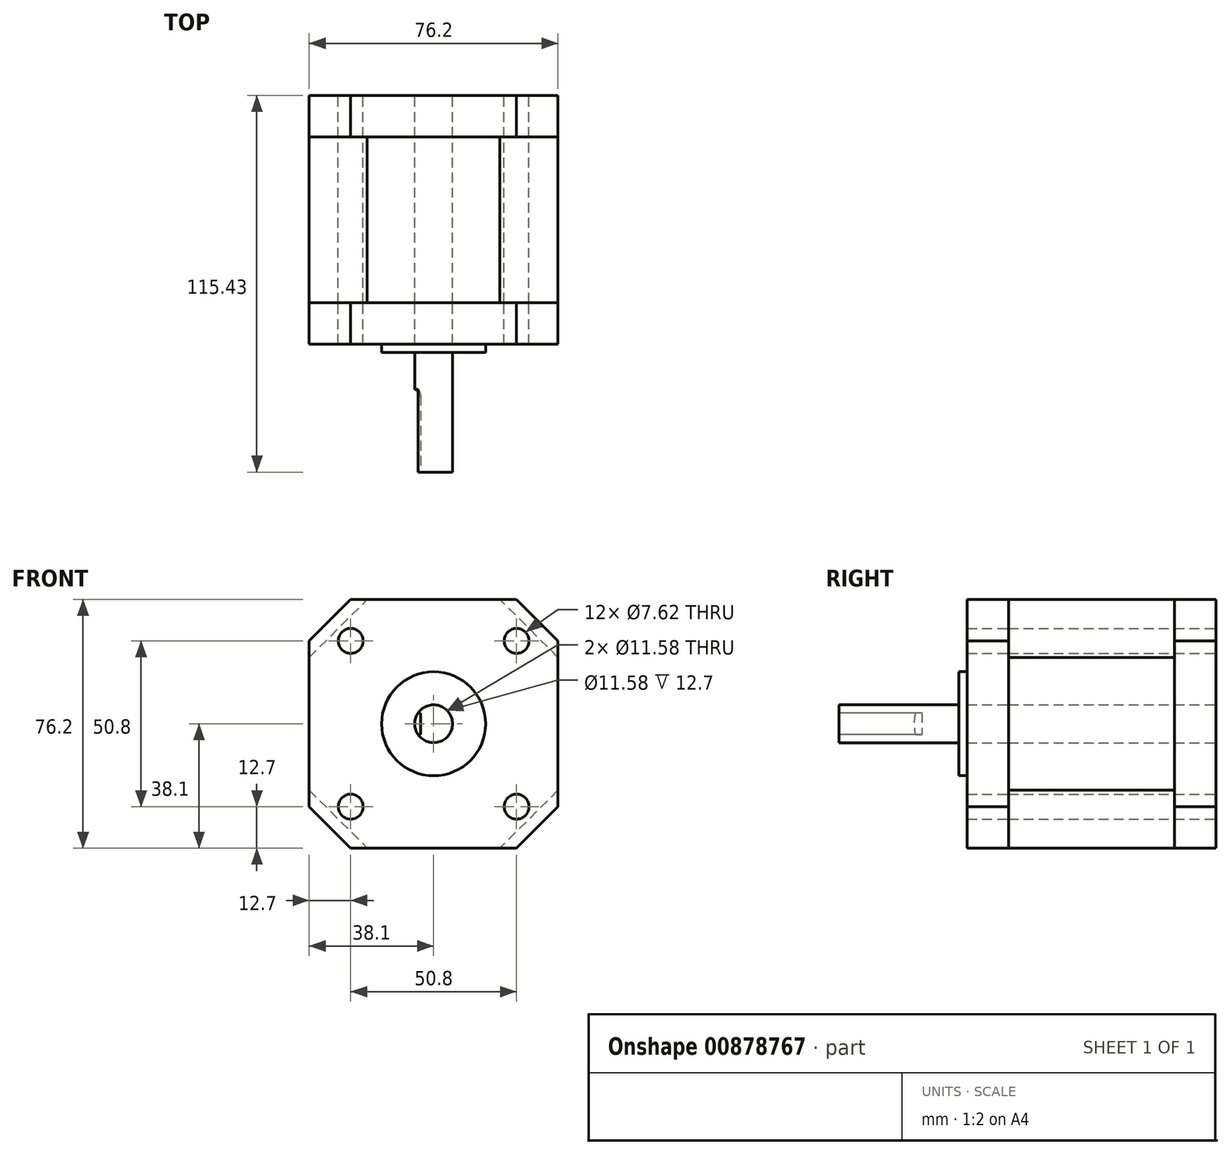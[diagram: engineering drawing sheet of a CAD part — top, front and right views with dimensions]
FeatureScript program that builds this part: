
annotation { "Feature Type Name" : "Feature", "Feature Type Description" : "" }
export const myFeature = defineFeature(function(context is Context, id is Id, definition is map)
    precondition{}
    {
        {
            var Q0;
            Q0=qCreatedBy(makeId("Front.planeOp"),FACE);
            var sketch = newSketch(context, id + "F0", { "sketchPlane" : qUnion([Q0])});
            skLineSegment(sketch, "E0.bottom", {"start": v(38.1, 38.1) * mm, "end": v(-38.1, 38.1) * mm});
            skLineSegment(sketch, "E0.top", {"start": v(38.1, -38.1) * mm, "end": v(-38.1, -38.1) * mm});
            skLineSegment(sketch, "E0.left", {"start": v(38.1, 38.1) * mm, "end": v(38.1, -38.1) * mm});
            skLineSegment(sketch, "E0.right", {"start": v(-38.1, 38.1) * mm, "end": v(-38.1, -38.1) * mm});
            skPoint(sketch, "E0.middle", {"position": v(0, 0) * mm});
            skLineSegment(sketch, "E1.bottom", {"start": v(25.4, -25.4) * mm, "end": v(-25.4, -25.4) * mm, "construction": true});
            skLineSegment(sketch, "E1.top", {"start": v(25.4, 25.4) * mm, "end": v(-25.4, 25.4) * mm, "construction": true});
            skLineSegment(sketch, "E1.left", {"start": v(25.4, -25.4) * mm, "end": v(25.4, 25.4) * mm, "construction": true});
            skLineSegment(sketch, "E1.right", {"start": v(-25.4, -25.4) * mm, "end": v(-25.4, 25.4) * mm, "construction": true});
            skCircle(sketch, "E2", {"center": v(25.4, 25.4) * mm, "radius": 3.81 * mm});
            skCircle(sketch, "E3", {"center": v(-25.4, 25.4) * mm, "radius": 3.81 * mm});
            skCircle(sketch, "E4", {"center": v(-25.4, -25.4) * mm, "radius": 3.81 * mm});
            skCircle(sketch, "E5", {"center": v(25.4, -25.4) * mm, "radius": 3.81 * mm});
            skCircle(sketch, "E6", {"center": v(25.4, 25.4) * mm, "radius": 7.62 * mm});
            skCircle(sketch, "E7", {"center": v(25.66, -25.26) * mm, "radius": 7.62 * mm});
            skCircle(sketch, "E8", {"center": v(-25.4, -25.4) * mm, "radius": 7.62 * mm});
            skCircle(sketch, "E9", {"center": v(-25.4, 25.4) * mm, "radius": 7.62 * mm});
            skCircle(sketch, "E10", {"center": v(0, 0) * mm, "radius": 5.79 * mm});
            skCircle(sketch, "E11", {"center": v(0, 0) * mm, "radius": 15.93 * mm});
            skSolve(sketch);
        }
        {
            var Q0;
            Q0=makeQuery(id+"F0.imprint","IMPRINT",FACE,{"disambiguationData":[TD([[makeQuery(id+"F0.imprint","IMPRINT",EDGE,{"derivedFrom":sQuery(id+"F0.wireOp",EDGE,"E10")}),-1.0]])]});
            var Q1;
            Q1=makeQuery(id+"F0.imprint","IMPRINT",FACE,{"disambiguationData":[TD([[makeQuery(id+"F0.imprint","IMPRINT",EDGE,{"derivedFrom":sQuery(id+"F0.wireOp",EDGE,"E0.bottom")}),1.0]])]});
            var Q2;
            Q2=makeQuery(id+"F0.imprint","IMPRINT",FACE,{"disambiguationData":[TD([[makeQuery(id+"F0.imprint","IMPRINT",EDGE,{"derivedFrom":sQuery(id+"F0.wireOp",EDGE,"E2")}),-1.0]])]});
            var Q3;
            Q3=makeQuery(id+"F0.imprint","IMPRINT",FACE,{"disambiguationData":[TD([[makeQuery(id+"F0.imprint","IMPRINT",EDGE,{"derivedFrom":sQuery(id+"F0.wireOp",EDGE,"E3")}),-1.0]])]});
            var Q4;
            Q4=makeQuery(id+"F0.imprint","IMPRINT",FACE,{"disambiguationData":[TD([[makeQuery(id+"F0.imprint","IMPRINT",EDGE,{"derivedFrom":sQuery(id+"F0.wireOp",EDGE,"E5")}),-1.0]])]});
            var Q5;
            Q5=makeQuery(id+"F0.imprint","IMPRINT",FACE,{"disambiguationData":[TD([[makeQuery(id+"F0.imprint","IMPRINT",EDGE,{"derivedFrom":sQuery(id+"F0.wireOp",EDGE,"E4")}),-1.0]])]});
            extrude(context, id + "F1", {"entities" : qUnion([Q0, Q1, Q2, Q3, Q4, Q5]), "depth" : 12.7 * mm, "offsetDistance" : 25.4 * mm});
        }
        {
            var Q0;
            Q0=makeQuery(id+"F1.opExtrude","CAP_FACE",FACE,{"disambiguationData":[OSD([sQuery(id+"F0.wireOp",EDGE,"E0.bottom"),sQuery(id+"F0.wireOp",EDGE,"E0.top"),sQuery(id+"F0.wireOp",EDGE,"E0.left"),sQuery(id+"F0.wireOp",EDGE,"E0.right"),sQuery(id+"F0.wireOp",EDGE,"E2"),sQuery(id+"F0.wireOp",EDGE,"E3"),sQuery(id+"F0.wireOp",EDGE,"E4"),sQuery(id+"F0.wireOp",EDGE,"E5"),sQuery(id+"F0.wireOp",EDGE,"E10")])],"isStart":false});
            extrude(context, id + "F2", {"entities" : qUnion([Q0]), "depth" : 50.8 * mm, "offsetDistance" : 25.4 * mm});
        }
        {
            var Q0;
            Q0=makeQuery(id+"F2.opExtrude","CAP_FACE",FACE,{"disambiguationData":[OSD([sQuery(id+"F0.wireOp",EDGE,"E0.bottom"),sQuery(id+"F0.wireOp",EDGE,"E0.top"),sQuery(id+"F0.wireOp",EDGE,"E0.left"),sQuery(id+"F0.wireOp",EDGE,"E0.right"),sQuery(id+"F0.wireOp",EDGE,"E2"),sQuery(id+"F0.wireOp",EDGE,"E3"),sQuery(id+"F0.wireOp",EDGE,"E4"),sQuery(id+"F0.wireOp",EDGE,"E5"),sQuery(id+"F0.wireOp",EDGE,"E10")])],"isStart":false});
            extrude(context, id + "F3", {"entities" : qUnion([Q0]), "depth" : 12.7 * mm, "offsetDistance" : 25.4 * mm});
        }
        {
            var Q0;
            Q0=makeQuery(id+"F3.opExtrude","CAP_FACE",FACE,{"disambiguationData":[OSD([sQuery(id+"F0.wireOp",EDGE,"E0.bottom"),sQuery(id+"F0.wireOp",EDGE,"E0.top"),sQuery(id+"F0.wireOp",EDGE,"E0.left"),sQuery(id+"F0.wireOp",EDGE,"E0.right"),sQuery(id+"F0.wireOp",EDGE,"E2"),sQuery(id+"F0.wireOp",EDGE,"E3"),sQuery(id+"F0.wireOp",EDGE,"E4"),sQuery(id+"F0.wireOp",EDGE,"E5"),sQuery(id+"F0.wireOp",EDGE,"E10")])],"isStart":false});
            var sketch = newSketch(context, id + "F4", { "sketchPlane" : qUnion([Q0])});
            skCircle(sketch, "E12.0", {"center": v(0, 0) * mm, "radius": 15.93 * mm});
            skSolve(sketch);
        }
        {
            var Q0;
            Q0=makeQuery(id+"F4.imprint","IMPRINT",FACE,{"disambiguationData":[TD([[makeQuery(id+"F4.imprint","IMPRINT",EDGE,{"derivedFrom":makeQuery(id+"F3.opExtrude","CAP_EDGE",EDGE,{"disambiguationData":[OSD([sQuery(id+"F0.wireOp",EDGE,"E10")])],"isStart":false})}),1.0]])]});
            var Q1;
            Q1=makeQuery(id+"F4.imprint","IMPRINT",FACE,{"disambiguationData":[TD([[makeQuery(id+"F4.imprint","IMPRINT",EDGE,{"derivedFrom":sQuery(id+"F4.wireOp",EDGE,"E12.0")}),1.0]])]});
            extrude(context, id + "F5", {"entities" : qUnion([Q0, Q1]), "operationType" : NewBodyOperationType.ADD, "depth" : 2.54 * mm, "offsetDistance" : 25.4 * mm});
        }
        {
            var Q0;
            Q0=makeQuery(id+"F5.opExtrude","CAP_FACE",FACE,{"disambiguationData":[OSD([sQuery(id+"F4.wireOp",EDGE,"E12.0")])],"isStart":false});
            var sketch = newSketch(context, id + "F6", { "sketchPlane" : qUnion([Q0])});
            skCircle(sketch, "E13.0", {"center": v(0, 0) * mm, "radius": 5.79 * mm});
            skSolve(sketch);
        }
        {
            var Q0;
            Q0=makeQuery(id+"F6.imprint","IMPRINT",FACE,{"disambiguationData":[TD([[makeQuery(id+"F6.imprint","IMPRINT",EDGE,{"derivedFrom":sQuery(id+"F6.wireOp",EDGE,"E13.0")}),1.0]])]});
            extrude(context, id + "F7", {"entities" : qUnion([Q0]), "depth" : 36.69 * mm, "offsetDistance" : 25.4 * mm});
        }
        {
            var Q0;
            Q0=makeQuery(id+"F3.opExtrude","SWEPT_EDGE",EDGE,{"disambiguationData":[OSD([sQuery(id+"F0.wireOp",EDGE,"E0.top"),sQuery(id+"F0.wireOp",EDGE,"E0.right")])]});
            var Q1;
            Q1=makeQuery(id+"F3.opExtrude","SWEPT_EDGE",EDGE,{"disambiguationData":[OSD([sQuery(id+"F0.wireOp",EDGE,"E0.bottom"),sQuery(id+"F0.wireOp",EDGE,"E0.right")])]});
            var Q2;
            Q2=makeQuery(id+"F1.opExtrude","SWEPT_EDGE",EDGE,{"disambiguationData":[OSD([sQuery(id+"F0.wireOp",EDGE,"E0.bottom"),sQuery(id+"F0.wireOp",EDGE,"E0.right")])]});
            var Q3;
            Q3=makeQuery(id+"F1.opExtrude","SWEPT_EDGE",EDGE,{"disambiguationData":[OSD([sQuery(id+"F0.wireOp",EDGE,"E0.top"),sQuery(id+"F0.wireOp",EDGE,"E0.right")])]});
            var Q4;
            Q4=makeQuery(id+"F1.opExtrude","SWEPT_EDGE",EDGE,{"disambiguationData":[OSD([sQuery(id+"F0.wireOp",EDGE,"E0.top"),sQuery(id+"F0.wireOp",EDGE,"E0.left")])]});
            var Q5;
            Q5=makeQuery(id+"F3.opExtrude","SWEPT_EDGE",EDGE,{"disambiguationData":[OSD([sQuery(id+"F0.wireOp",EDGE,"E0.top"),sQuery(id+"F0.wireOp",EDGE,"E0.left")])]});
            var Q6;
            Q6=makeQuery(id+"F1.opExtrude","SWEPT_EDGE",EDGE,{"disambiguationData":[OSD([sQuery(id+"F0.wireOp",EDGE,"E0.bottom"),sQuery(id+"F0.wireOp",EDGE,"E0.left")])]});
            var Q7;
            Q7=makeQuery(id+"F3.opExtrude","SWEPT_EDGE",EDGE,{"disambiguationData":[OSD([sQuery(id+"F0.wireOp",EDGE,"E0.bottom"),sQuery(id+"F0.wireOp",EDGE,"E0.left")])]});
            chamfer(context, id + "F8", {"entities" : qUnion([Q0, Q1, Q2, Q3, Q4, Q5, Q6, Q7]), "width" : 12.7 * mm, "tangentPropagation" : true});
        }
        {
            var Q0;
            Q0=makeQuery(id+"F2.opExtrude","SWEPT_EDGE",EDGE,{"disambiguationData":[OSD([sQuery(id+"F0.wireOp",EDGE,"E0.top"),sQuery(id+"F0.wireOp",EDGE,"E0.left")])]});
            var Q1;
            Q1=makeQuery(id+"F2.opExtrude","SWEPT_EDGE",EDGE,{"disambiguationData":[OSD([sQuery(id+"F0.wireOp",EDGE,"E0.bottom"),sQuery(id+"F0.wireOp",EDGE,"E0.left")])]});
            var Q2;
            Q2=makeQuery(id+"F2.opExtrude","SWEPT_EDGE",EDGE,{"disambiguationData":[OSD([sQuery(id+"F0.wireOp",EDGE,"E0.bottom"),sQuery(id+"F0.wireOp",EDGE,"E0.right")])]});
            var Q3;
            Q3=makeQuery(id+"F2.opExtrude","SWEPT_EDGE",EDGE,{"disambiguationData":[OSD([sQuery(id+"F0.wireOp",EDGE,"E0.top"),sQuery(id+"F0.wireOp",EDGE,"E0.right")])]});
            chamfer(context, id + "F9", {"entities" : qUnion([Q0, Q1, Q2, Q3]), "width" : 17.78 * mm, "tangentPropagation" : true});
        }
        {
            var Q0;
            Q0=makeQuery(id+"F7.opExtrude","CAP_FACE",FACE,{"disambiguationData":[OSD([sQuery(id+"F6.wireOp",EDGE,"E13.0")])],"isStart":false});
            var sketch = newSketch(context, id + "F10", { "sketchPlane" : qUnion([Q0])});
            skLineSegment(sketch, "E14.bottom", {"start": v(-4.04, 3.32) * mm, "end": v(-7.54, 3.32) * mm});
            skLineSegment(sketch, "E14.top", {"start": v(-4.04, -3.32) * mm, "end": v(-7.54, -3.32) * mm});
            skLineSegment(sketch, "E14.left", {"start": v(-4.04, 3.32) * mm, "end": v(-4.04, -3.32) * mm});
            skLineSegment(sketch, "E14.right", {"start": v(-7.54, 3.32) * mm, "end": v(-7.54, -3.32) * mm});
            skPoint(sketch, "E14.middle", {"position": v(-5.79, 0) * mm});
            skSolve(sketch);
        }
        {
            var Q0;
            {var subQ0=sQuery(id+"F10.wireOp",EDGE,"E14.left");Q0=makeQuery(id+"F10.imprint","IMPRINT",FACE,{"disambiguationData":[TD([[makeQuery(id+"F10.imprint","IMPRINT",EDGE,{"derivedFrom":subQ0}),-1.0]])]});}
            extrude(context, id + "F11", {"entities" : qUnion([Q0]), "operationType" : NewBodyOperationType.REMOVE, "oppositeDirection" : true, "depth" : 25.4 * mm, "offsetDistance" : 25.4 * mm});
        }
        {
            var Q0;
            Q0=makeQuery(id+"F11.boolean.opBoolean","COPY",EDGE,{"derivedFrom":makeQuery(id+"F11.opExtrude","CAP_EDGE",EDGE,{"disambiguationData":[OSD([sQuery(id+"F10.wireOp",EDGE,"E14.left")])],"isStart":false})});
            fillet(context, id + "F12", {"entities" : qUnion([Q0]), "radius" : 2.54 * mm, "tangentPropagation" : true, "allowEdgeOverflow" : false});
        }
    });
